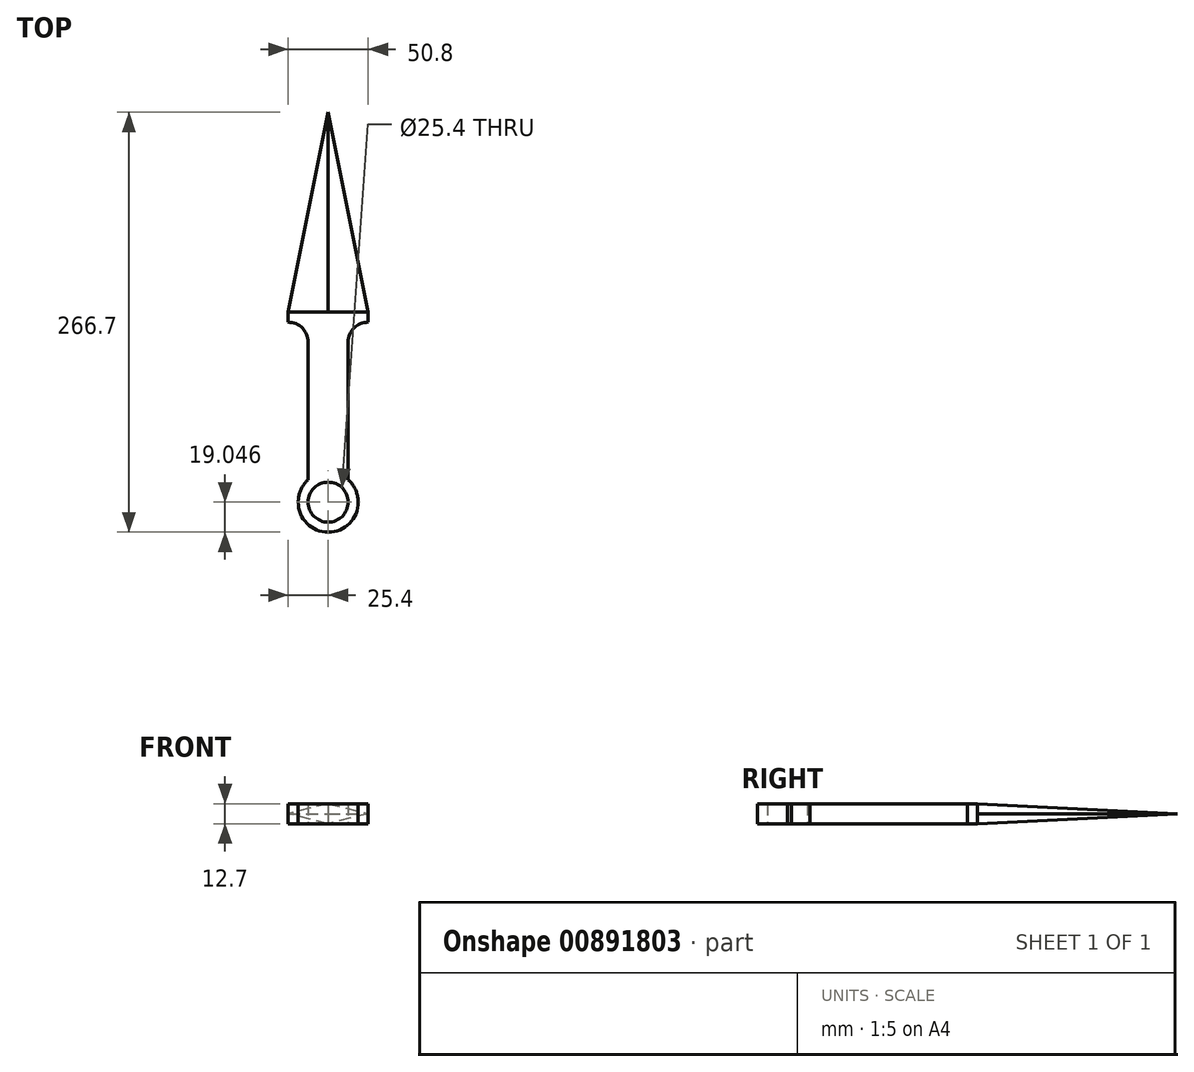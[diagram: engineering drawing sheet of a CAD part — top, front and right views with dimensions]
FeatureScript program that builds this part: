
annotation { "Feature Type Name" : "Feature", "Feature Type Description" : "" }
export const myFeature = defineFeature(function(context is Context, id is Id, definition is map)
    precondition{}
    {
        {
            var Q0;
            Q0=qCreatedBy(makeId("Top.planeOp"),FACE);
            var sketch = newSketch(context, id + "F0", { "sketchPlane" : qUnion([Q0])});
            skCircle(sketch, "E0", {"center": v(0, -62.8) * mm, "radius": 12.7 * mm});
            skCircle(sketch, "E1", {"center": v(0, -62.8) * mm, "radius": 19.05 * mm});
            skLineSegment(sketch, "E2", {"start": v(-19.05, -62.8) * mm, "end": v(-12.7, 38.8) * mm});
            skLineSegment(sketch, "E3", {"start": v(19.05, -62.8) * mm, "end": v(12.7, 38.8) * mm});
            skLineSegment(sketch, "E4", {"start": v(12.7, 38.8) * mm, "end": v(-12.7, 38.8) * mm});
            skLineSegment(sketch, "E5", {"start": v(-12.7, -62.8) * mm, "end": v(-12.7, 38.8) * mm});
            skLineSegment(sketch, "E6", {"start": v(12.7, -62.8) * mm, "end": v(12.7, 38.8) * mm});
            skLineSegment(sketch, "E7", {"start": v(-12.7, 38.8) * mm, "end": v(-12.7, 38.8) * mm});
            skLineSegment(sketch, "E8", {"start": v(-25.4, 51.5) * mm, "end": v(-25.4, 51.5) * mm});
            skLineSegment(sketch, "E9", {"start": v(12.7, 38.8) * mm, "end": v(12.7, 38.8) * mm});
            skLineSegment(sketch, "E10", {"start": v(25.4, 51.5) * mm, "end": v(25.4, 51.5) * mm});
            skLineSegment(sketch, "E11", {"start": v(-25.4, 51.5) * mm, "end": v(-25.4, 57.85) * mm});
            skLineSegment(sketch, "E12", {"start": v(-25.4, 57.85) * mm, "end": v(25.4, 57.85) * mm});
            skLineSegment(sketch, "E13", {"start": v(25.4, 57.85) * mm, "end": v(25.4, 51.5) * mm});
            skPoint(sketch, "E14.visualSharp", {"position": v(-12.7, 51.5) * mm});
            skArc(sketch, "E14.filletArc", {"start": v(-12.7, 38.8) * mm, "mid": v(-16.42, 47.78) * mm, "end": v(-25.4, 51.5) * mm});
            skPoint(sketch, "E15.visualSharp", {"position": v(12.7, 51.5) * mm});
            skArc(sketch, "E15.filletArc", {"start": v(25.4, 51.5) * mm, "mid": v(16.42, 47.78) * mm, "end": v(12.7, 38.8) * mm});
            skLineSegment(sketch, "E16", {"start": v(0, 57.85) * mm, "end": v(0, 184.85) * mm});
            skLineSegment(sketch, "E17", {"start": v(0, 184.85) * mm, "end": v(25.4, 57.85) * mm});
            skLineSegment(sketch, "E18", {"start": v(-25.4, 57.85) * mm, "end": v(0, 184.85) * mm});
            skSolve(sketch);
        }
        {
            var Q0;
            Q0=makeQuery(id+"F0.imprint","IMPRINT",FACE,{"disambiguationData":[TD([[makeQuery(id+"F0.imprint","IMPRINT",EDGE,{"derivedFrom":sQuery(id+"F0.wireOp",EDGE,"E4")}),-1.0]])]});
            var Q1;
            {var subQ5=sQuery(id+"F0.wireOp",EDGE,"E4");Q1=makeQuery(id+"F0.imprint","IMPRINT",FACE,{"disambiguationData":[TD([[makeQuery(id+"F0.imprint","IMPRINT",EDGE,{"derivedFrom":subQ5}),1.0]])]});}
            var Q2;
            {var subQ0=sQuery(id+"F0.wireOp",EDGE,"E2");var subQ1=sQuery(id+"F0.wireOp",EDGE,"E1");var subQ2=makeQuery(id+"F0.imprint","INTERSECT",VERTEX,{"disambiguationData":[OD(1.0)],"derivedFrom":[subQ1,subQ0]});Q2=makeQuery(id+"F0.imprint","IMPRINT",FACE,{"disambiguationData":[TD([[makeQuery(id+"F0.imprint","IMPRINT",EDGE,{"disambiguationData":[TD([[subQ2,1.0]])],"derivedFrom":subQ1}),-1.0]])]});}
            var Q3;
            {var subQ0=sQuery(id+"F0.wireOp",EDGE,"E3");var subQ1=sQuery(id+"F0.wireOp",EDGE,"E1");var subQ2=makeQuery(id+"F0.imprint","INTERSECT",VERTEX,{"disambiguationData":[OD(1.0)],"derivedFrom":[subQ1,subQ0]});Q3=makeQuery(id+"F0.imprint","IMPRINT",FACE,{"disambiguationData":[TD([[makeQuery(id+"F0.imprint","IMPRINT",EDGE,{"disambiguationData":[TD([[subQ2,-1.0]])],"derivedFrom":subQ1}),-1.0]])]});}
            var Q4;
            {var subQ6=sQuery(id+"F0.wireOp",EDGE,"E5");var subQ11=sQuery(id+"F0.wireOp",EDGE,"E0");var subQ12=makeQuery(id+"F0.imprint","INTERSECT",VERTEX,{"derivedFrom":[subQ11,subQ6]});Q4=makeQuery(id+"F0.imprint","IMPRINT",FACE,{"disambiguationData":[TD([[makeQuery(id+"F0.imprint","IMPRINT",EDGE,{"disambiguationData":[TD([[subQ12,-1.0]])],"derivedFrom":subQ11}),-1.0]])]});}
            var Q5;
            {var subQ0=sQuery(id+"F0.wireOp",EDGE,"E5");var subQ1=sQuery(id+"F0.wireOp",EDGE,"E0");var subQ2=makeQuery(id+"F0.imprint","INTERSECT",VERTEX,{"derivedFrom":[subQ1,subQ0]});Q5=makeQuery(id+"F0.imprint","IMPRINT",FACE,{"disambiguationData":[TD([[makeQuery(id+"F0.imprint","IMPRINT",EDGE,{"disambiguationData":[TD([[subQ2,1.0]])],"derivedFrom":subQ1}),-1.0]])]});}
            extrude(context, id + "F1", {"entities" : qUnion([Q0, Q1, Q2, Q3, Q4, Q5]), "endBound" : BoundingType.SYMMETRIC, "depth" : 12.7 * mm, "offsetDistance" : 25.4 * mm});
        }
        {
            var Q0;
            Q0=makeQuery(id+"F1.opExtrude","CAP_EDGE",EDGE,{"disambiguationData":[OSD([sQuery(id+"F0.wireOp",EDGE,"E12")])],"isStart":false});
            cPoint(context, id + "F2", {"entities" : qUnion([Q0]), "parameter" : 0.5});
        }
        {
            var Q0;
            Q0 = qCreatedBy(id + "F2" ,VERTEX);
            var Q1;
            Q1=sQuery(id+"F0.wireOp",VERTEX,"E11.end");
            var Q2;
            Q2=sQuery(id+"F0.wireOp",VERTEX,"E16.end");
            cPlane(context, id + "F3", {"entities" : qUnion([Q0, Q1, Q2]), "cplaneType" : CPlaneType.THREE_POINT, "offset" : 25.4 * mm, "width" : 152.4 * mm, "height" : 152.4 * mm});
        }
        {
            var Q0;
            Q0=qCreatedBy(id+"F3.planeOp",FACE);
            var sketch = newSketch(context, id + "F4", { "sketchPlane" : qUnion([Q0])});
            skLineSegment(sketch, "E19", {"start": v(-23.94, 57.77) * mm, "end": v(2.24, 184.62) * mm});
            skLineSegment(sketch, "E20", {"start": v(2.24, 184.62) * mm, "end": v(2.24, 57.46) * mm});
            skLineSegment(sketch, "E21", {"start": v(2.24, 57.46) * mm, "end": v(-23.94, 57.77) * mm});
            skSolve(sketch);
        }
        {
            var Q0;
            Q0=sQuery(id+"F4.wireOp",VERTEX,"E20.end");
            var Q1;
            Q1=sQuery(id+"F0.wireOp",VERTEX,"E12.end");
            var Q2;
            Q2=sQuery(id+"F0.wireOp",VERTEX,"E16.end");
            cPlane(context, id + "F5", {"entities" : qUnion([Q0, Q1, Q2]), "cplaneType" : CPlaneType.THREE_POINT, "offset" : 25.4 * mm, "width" : 152.4 * mm, "height" : 152.4 * mm});
        }
        {
            var Q0;
            Q0=qCreatedBy(id+"F5.planeOp",FACE);
            var sketch = newSketch(context, id + "F6", { "sketchPlane" : qUnion([Q0])});
            skLineSegment(sketch, "E22", {"start": v(-2.24, -184.62) * mm, "end": v(23.94, -57.77) * mm});
            skLineSegment(sketch, "E23", {"start": v(-2.24, -57.46) * mm, "end": v(-2.24, -184.62) * mm});
            skLineSegment(sketch, "E24", {"start": v(-2.24, -57.46) * mm, "end": v(23.94, -57.77) * mm});
            skSolve(sketch);
        }
        {
            var Q0;
            Q0=makeQuery(id+"F1.opExtrude","CAP_EDGE",EDGE,{"disambiguationData":[OSD([sQuery(id+"F0.wireOp",EDGE,"E12")])],"isStart":true});
            cPoint(context, id + "F7", {"entities" : qUnion([Q0]), "parameter" : 0.5});
        }
        {
            var Q0;
            Q0 = qCreatedBy(id + "F7" ,VERTEX);
            var Q1;
            Q1=sQuery(id+"F0.wireOp",VERTEX,"E12.end");
            var Q2;
            Q2=sQuery(id+"F0.wireOp",VERTEX,"E16.end");
            cPlane(context, id + "F8", {"entities" : qUnion([Q0, Q1, Q2]), "cplaneType" : CPlaneType.THREE_POINT, "offset" : 25.4 * mm, "width" : 152.4 * mm, "height" : 152.4 * mm});
        }
        {
            var Q0;
            Q0=qCreatedBy(id+"F8.planeOp",FACE);
            var sketch = newSketch(context, id + "F9", { "sketchPlane" : qUnion([Q0])});
            skLineSegment(sketch, "E25", {"start": v(-2.24, -184.62) * mm, "end": v(23.94, -57.77) * mm});
            skLineSegment(sketch, "E26", {"start": v(-2.24, -57.46) * mm, "end": v(-2.24, -184.62) * mm});
            skLineSegment(sketch, "E27", {"start": v(23.94, -57.77) * mm, "end": v(-2.24, -57.46) * mm});
            skSolve(sketch);
        }
        {
            var Q0;
            Q0=makeQuery(id+"F1.opExtrude","CAP_EDGE",EDGE,{"disambiguationData":[OSD([sQuery(id+"F0.wireOp",EDGE,"E12")])],"isStart":true});
            cPoint(context, id + "F10", {"entities" : qUnion([Q0]), "parameter" : 0.5});
        }
        {
            var Q0;
            Q0=sQuery(id+"F0.wireOp",VERTEX,"E16.end");
            var Q1;
            Q1=sQuery(id+"F0.wireOp",VERTEX,"E11.end");
            var Q2;
            Q2 = qCreatedBy(id + "F10" ,VERTEX);
            cPlane(context, id + "F11", {"entities" : qUnion([Q0, Q1, Q2]), "cplaneType" : CPlaneType.THREE_POINT, "offset" : 25.4 * mm, "width" : 152.4 * mm, "height" : 152.4 * mm});
        }
        {
            var Q0;
            Q0=qCreatedBy(id+"F11.planeOp",FACE);
            var sketch = newSketch(context, id + "F12", { "sketchPlane" : qUnion([Q0])});
            skLineSegment(sketch, "E28", {"start": v(2.24, -57.46) * mm, "end": v(-23.94, -57.77) * mm});
            skLineSegment(sketch, "E29", {"start": v(-23.94, -57.77) * mm, "end": v(2.24, -184.62) * mm});
            skLineSegment(sketch, "E30", {"start": v(2.24, -184.62) * mm, "end": v(2.24, -57.46) * mm});
            skSolve(sketch);
        }
        {
            var Q1;
            Q1=makeQuery(id+"F6.imprint","IMPRINT",FACE,{"disambiguationData":[TD([[makeQuery(id+"F6.imprint","IMPRINT",EDGE,{"derivedFrom":sQuery(id+"F6.wireOp",EDGE,"E22")}),1.0]])]});
            var Q2;
            Q2=makeQuery(id+"F12.imprint","IMPRINT",FACE,{"disambiguationData":[TD([[makeQuery(id+"F12.imprint","IMPRINT",EDGE,{"derivedFrom":sQuery(id+"F12.wireOp",EDGE,"E28")}),1.0]])]});
            loft(context, id + "F13", {"sheetProfilesArray" : [{ "sheetProfileEntities" : qUnion([Q1]) }, { "sheetProfileEntities" : qUnion([Q2]) }]});
        }
    });
